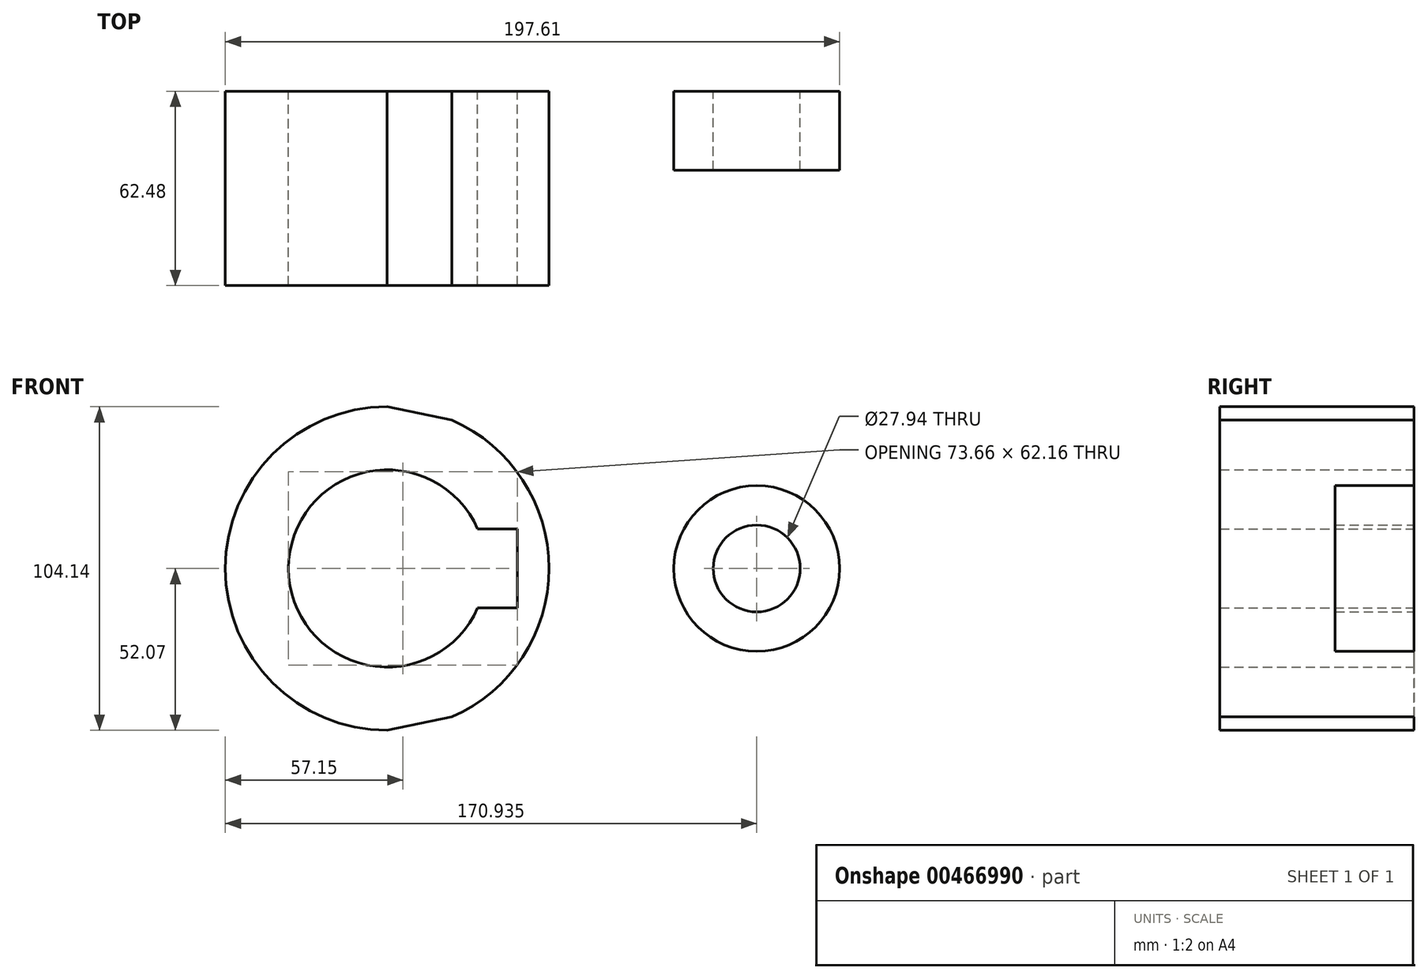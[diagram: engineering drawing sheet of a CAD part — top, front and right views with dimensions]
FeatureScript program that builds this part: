
annotation { "Feature Type Name" : "Feature", "Feature Type Description" : "" }
export const myFeature = defineFeature(function(context is Context, id is Id, definition is map)
    precondition{}
    {
        {
            var Q0;
            Q0=qCreatedBy(makeId("Front.planeOp"),FACE);
            var sketch = newSketch(context, id + "F0", { "sketchPlane" : qUnion([Q0])});
            skCircle(sketch, "E0", {"center": v(0, 0) * mm, "radius": 52.07 * mm});
            skCircle(sketch, "E1", {"center": v(118.87, 0) * mm, "radius": 26.67 * mm});
            skLineSegment(sketch, "E2", {"start": v(0, 52.07) * mm, "end": v(124.32, 26.1) * mm});
            skLineSegment(sketch, "E3", {"start": v(0, -52.07) * mm, "end": v(124.32, -26.1) * mm});
            skCircle(sketch, "E4", {"center": v(0, 0) * mm, "radius": 31.75 * mm});
            skCircle(sketch, "E5", {"center": v(118.87, 0) * mm, "radius": 13.97 * mm});
            skLineSegment(sketch, "E6.bottom", {"start": v(-41.91, -12.7) * mm, "end": v(41.91, -12.7) * mm});
            skLineSegment(sketch, "E6.top", {"start": v(-41.91, 12.7) * mm, "end": v(41.91, 12.7) * mm});
            skLineSegment(sketch, "E6.left", {"start": v(-41.91, -12.7) * mm, "end": v(-41.91, 12.7) * mm});
            skLineSegment(sketch, "E6.right", {"start": v(41.91, -12.7) * mm, "end": v(41.91, 12.7) * mm});
            skSolve(sketch);
        }
        {
            var Q0;
            {var subQ0=sQuery(id+"F0.wireOp",EDGE,"E2");var subQ1=sQuery(id+"F0.wireOp",EDGE,"E0");var subQ2=makeQuery(id+"F0.imprint","INTERSECT",VERTEX,{"disambiguationData":[OD(1.0)],"derivedFrom":[subQ1,subQ0]});Q0=makeQuery(id+"F0.imprint","IMPRINT",FACE,{"disambiguationData":[TD([[makeQuery(id+"F0.imprint","IMPRINT",EDGE,{"disambiguationData":[TD([[subQ2,1.0]])],"derivedFrom":subQ1}),-1.0]])]});}
            var Q1;
            {var subQ4=sQuery(id+"F0.wireOp",EDGE,"E6.left");Q1=makeQuery(id+"F0.imprint","IMPRINT",FACE,{"disambiguationData":[TD([[makeQuery(id+"F0.imprint","IMPRINT",EDGE,{"derivedFrom":subQ4}),1.0]])]});}
            var Q2;
            {var subQ5=sQuery(id+"F0.wireOp",EDGE,"E6.left");Q2=makeQuery(id+"F0.imprint","IMPRINT",FACE,{"disambiguationData":[TD([[makeQuery(id+"F0.imprint","IMPRINT",EDGE,{"derivedFrom":subQ5}),-1.0]])]});}
            var Q3;
            Q3=makeQuery(id+"F0.imprint","IMPRINT",FACE,{"disambiguationData":[TD([[makeQuery(id+"F0.imprint","IMPRINT",EDGE,{"derivedFrom":sQuery(id+"F0.wireOp",EDGE,"E5")}),-1.0]])]});
            extrude(context, id + "F1", {"entities" : qUnion([Q0, Q1, Q2, Q3]), "depth" : 25.4 * mm});
        }
        {
            var Q0;
            {var subQ4=sQuery(id+"F0.wireOp",EDGE,"E6.left");Q0=makeQuery(id+"F0.imprint","IMPRINT",FACE,{"disambiguationData":[TD([[makeQuery(id+"F0.imprint","IMPRINT",EDGE,{"derivedFrom":subQ4}),1.0]])]});}
            var Q1;
            {var subQ5=sQuery(id+"F0.wireOp",EDGE,"E6.left");Q1=makeQuery(id+"F0.imprint","IMPRINT",FACE,{"disambiguationData":[TD([[makeQuery(id+"F0.imprint","IMPRINT",EDGE,{"derivedFrom":subQ5}),-1.0]])]});}
            extrude(context, id + "F2", {"entities" : qUnion([Q0, Q1]), "operationType" : NewBodyOperationType.ADD, "depth" : 62.48 * mm});
        }
    });
